# Revit family: E758
name_source: partatom
category: Communication Devices
revit_build: Autodesk Revit 2018 (Build: 20170223_1515(x64)
units: mm (PartAtom-declared; Revit-internal decimal feet)

## family parameters
Always vertical = Yes
Cut with Voids When Loaded = No
Maintain Annotation Orientation = No
Part Type = Normal
Room Calculation Point = No
Round Connector Dimension = Use Diameter
Shared = No
Work Plane-Based = No

## types (1)
- E758
    ADDITIONAL FEATURES = Integrated USB Media Player, Variable picture modes (Dynamic/Standard/Energy Savings/Conferencing/HighBright/Custom/HDR), Advanced Video/Audio Settings, HDR 10 Support, Variable Sound Modes (Standard/Music/Movie/Custom), CEC Communication, First and Custom Detect Options, Sleep Timer, Built-In closed captioning, Integrated Ambien Light Sensor, Integrated Temperature Sensors, Local Dimming, Power USB (5V/3A)Amx/CEC/Crestron Connected SupportJoy Stick (Key Guide)NaViSet Administrator 2 CompatibleLAN or RS232 Communication (limited), USB-C Port for power delivery
    CONNECTIVITY- Input Terminals- Analog = VGA 15-pin D-Sub, Stereo Mini Jack 3.5mm
    CONNECTIVITY- Input Terminals- Audio = Digital Audio through HDMI x 3, Stereo Mini Jack
    CONNECTIVITY- Input Terminals- Data = USB 2.0 (Media Player Auto Playback)
    CONNECTIVITY- Input Terminals- Digital = HDMI (2.0 x 3 with HDCP 2.2)
    CONNECTIVITY- Input Terminals- External Control = RS-232C, LAN (100Mb) with limitation
    CONNECTIVITY- Output Terminals- Audio Amplifier = Stereo Mini Jack 3.5mm
    CONNECTIVITY- Output Terminals- USB Type-C Power Delivery = 5V/3A
    ENVIRONMENTAL CONDITIONS- Operating Altitude = 3000m (9843ft)
    ENVIRONMENTAL CONDITIONS- Operating Humidity = 20-80%
    ENVIRONMENTAL CONDITIONS- Operating Temperature = 32-104°F / 0-40°C
    LCD MODULE- Aspect Ratio = 16:9
    LCD MODULE- Brightness (Typical/Minimum) = 350 cd/m2
    LCD MODULE- Color Gamut = '72% NTSC
    LCD MODULE- Contrast Ratio (Typical)* = '1200:1 (without local dimming)
    LCD MODULE- Displayable Colors = Over 1.07 Billion (10bit)
    LCD MODULE- Native Resolution = 3840 x 2160
    LCD MODULE- Orientation = Landscape and Portrait
    LCD MODULE- Panel Haze (%) = 25
    LCD MODULE- Panel Technology = IPS
    LCD MODULE- Viewable Image Size = 75in.
    LCD MODULE- Viewing Angle = 178° Vert., 178° Hor. (89U/89D/89L/89R) @ CR>10
    LIMITED WARRANTY = 3 years Advanced Replacement
    Manufacturer = NEC Display Solutions
    Model = E758
    Optional Stand = ST-801
    Other Accessories = Table Top Stand (ST-801), Tilt Wall Mount (WMK-7598T)
    PHYSICAL SPECS- Bezel Width (L/R, T/B) = 14.3 x 14.3 x 14.3 x 14.8mm
    PHYSICAL SPECS- Net Dimensions (Without stand, W x H x D) = 1682.30 x 961.10 x 83.2mm (66.23 x 37.84 x 3.28 in.)
    PHYSICAL SPECS- Net Weight (Without Stand) = 80.0 lbs. / 36.30kg
    PHYSICAL SPECS- VESA Hole Configuration = 600 x 400mm (M8)
    POWER CONSUMPTION- Current Rating = 1.2A - 2.8A @ 100V - 240V
    POWER CONSUMPTION- Network Standby = 2W
    POWER CONSUMPTION- Normal Standby = 0.5W
    POWER CONSUMPTION- On (Typ/Max Brightness/All Max) = 145W/180W/250W
    POWER CONSUMPTION- Speaker Rating = Integrated 10W x 10W
    SENSORS- Ambient Light Sensor = Integrated
    SENSORS- Temperature Sensor = Internal Sensors
    SHIPS WITH = Power Cord, 3.0m HDMI Cable, Wireless Remote Control, Batteries, Setup Manual
    URL = www.necdisplay.com

## geometry (parser evidence)
native form markers: Sweep x3
no freeform markers — native parametric forms only
